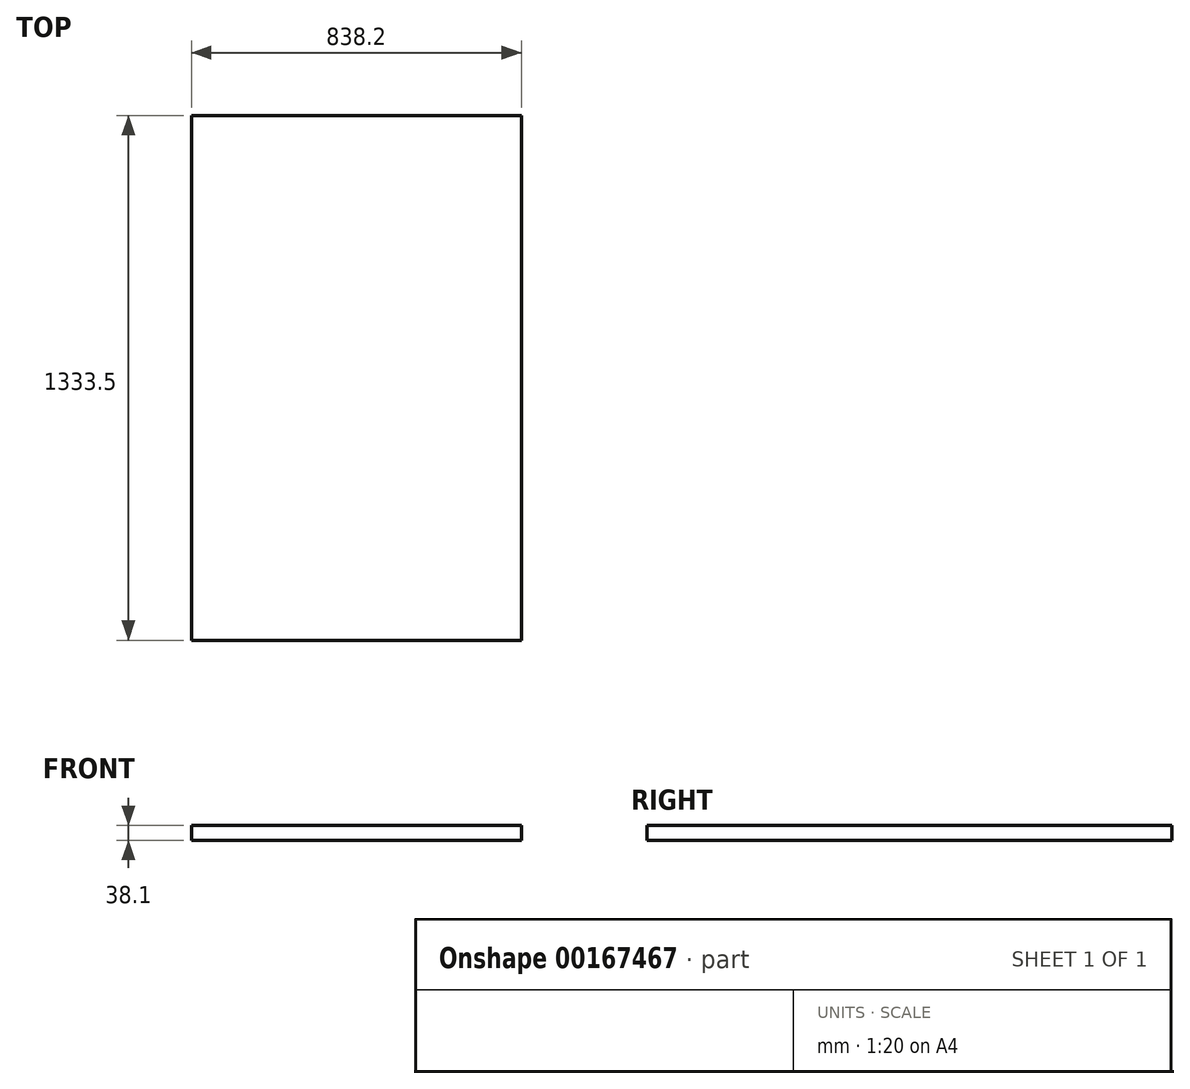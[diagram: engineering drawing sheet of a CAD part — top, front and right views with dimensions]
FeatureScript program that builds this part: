
annotation { "Feature Type Name" : "Feature", "Feature Type Description" : "" }
export const myFeature = defineFeature(function(context is Context, id is Id, definition is map)
    precondition{}
    {
        {
            var Q0;
            Q0=qCreatedBy(makeId("Top.planeOp"),FACE);
            var sketch = newSketch(context, id + "F0", { "sketchPlane" : qUnion([Q0])});
            skLineSegment(sketch, "E0.bottom", {"start": v(-419.1, 666.75) * mm, "end": v(419.1, 666.75) * mm});
            skLineSegment(sketch, "E0.top", {"start": v(-419.1, -666.75) * mm, "end": v(419.1, -666.75) * mm});
            skLineSegment(sketch, "E0.left", {"start": v(-419.1, 666.75) * mm, "end": v(-419.1, -666.75) * mm});
            skLineSegment(sketch, "E0.right", {"start": v(419.1, 666.75) * mm, "end": v(419.1, -666.75) * mm});
            skPoint(sketch, "E0.middle", {"position": v(0, 0) * mm});
            skLineSegment(sketch, "E1.bottom", {"start": v(-381, 628.65) * mm, "end": v(381, 628.65) * mm});
            skLineSegment(sketch, "E1.top", {"start": v(-381, -628.65) * mm, "end": v(381, -628.65) * mm});
            skLineSegment(sketch, "E1.left", {"start": v(-381, 628.65) * mm, "end": v(-381, -628.65) * mm});
            skLineSegment(sketch, "E1.right", {"start": v(381, 628.65) * mm, "end": v(381, -628.65) * mm});
            skSolve(sketch);
        }
        {
            var Q0;
            Q0=makeQuery(id+"F0.imprint","IMPRINT",FACE,{"disambiguationData":[TD([[makeQuery(id+"F0.imprint","IMPRINT",EDGE,{"derivedFrom":sQuery(id+"F0.wireOp",EDGE,"E0.bottom")}),-1.0]])]});
            var Q1;
            Q1=makeQuery(id+"F0.imprint","IMPRINT",FACE,{"disambiguationData":[TD([[makeQuery(id+"F0.imprint","IMPRINT",EDGE,{"derivedFrom":sQuery(id+"F0.wireOp",EDGE,"E1.bottom")}),-1.0]])]});
            extrude(context, id + "F1", {"entities" : qUnion([Q0, Q1]), "depth" : 38.1 * mm});
        }
    });
